# Revit family: Access_Door-Recessed-Cendrex-With_Exposed_Flange-AHRz
name_source: partatom
category: Specialty Equipment
units: mm (PartAtom-declared; Revit-internal decimal feet)

## family parameters
Cut with Voids When Loaded = No
Enable Cutting in Views = No
Host = Face
Maintain Annotation Orientation = No
OmniClass Number = 23.30.10.27.17
OmniClass Title = Access Doors
Part Type = Normal
Room Calculation Point = No
Round Connector Dimension = Use Diameter
Shared = No

## types (1)
- Default - please load Revit Family Type Catalog
    Assembly Code = C1030.80
    Available Options = http://cendrex.com
    Cendrex LEED Ready Program = http://www.cendrex.com
    Construction Material = Metal - Cendrex - Stainless Steel
    Default Elevation = 0 "
    Description = Flush universal removable access door with exposed flange
    Finish = Metal - Cendrex - Powder Coated White
    Frame Depth = 2 "
    Height = 48 "
    Height Calc = 48 "
    Keynote = 08 10 00
    Manufacturer = Cendrex
    Model = AHR
    URL = http://www.cendrex.com
    Version = 1
    Weight = 0.00 lb
    Width = 48 "
    Width Calc = 48 "

## geometry (parser evidence)
native form markers: Sweep x7
no freeform markers — native parametric forms only
